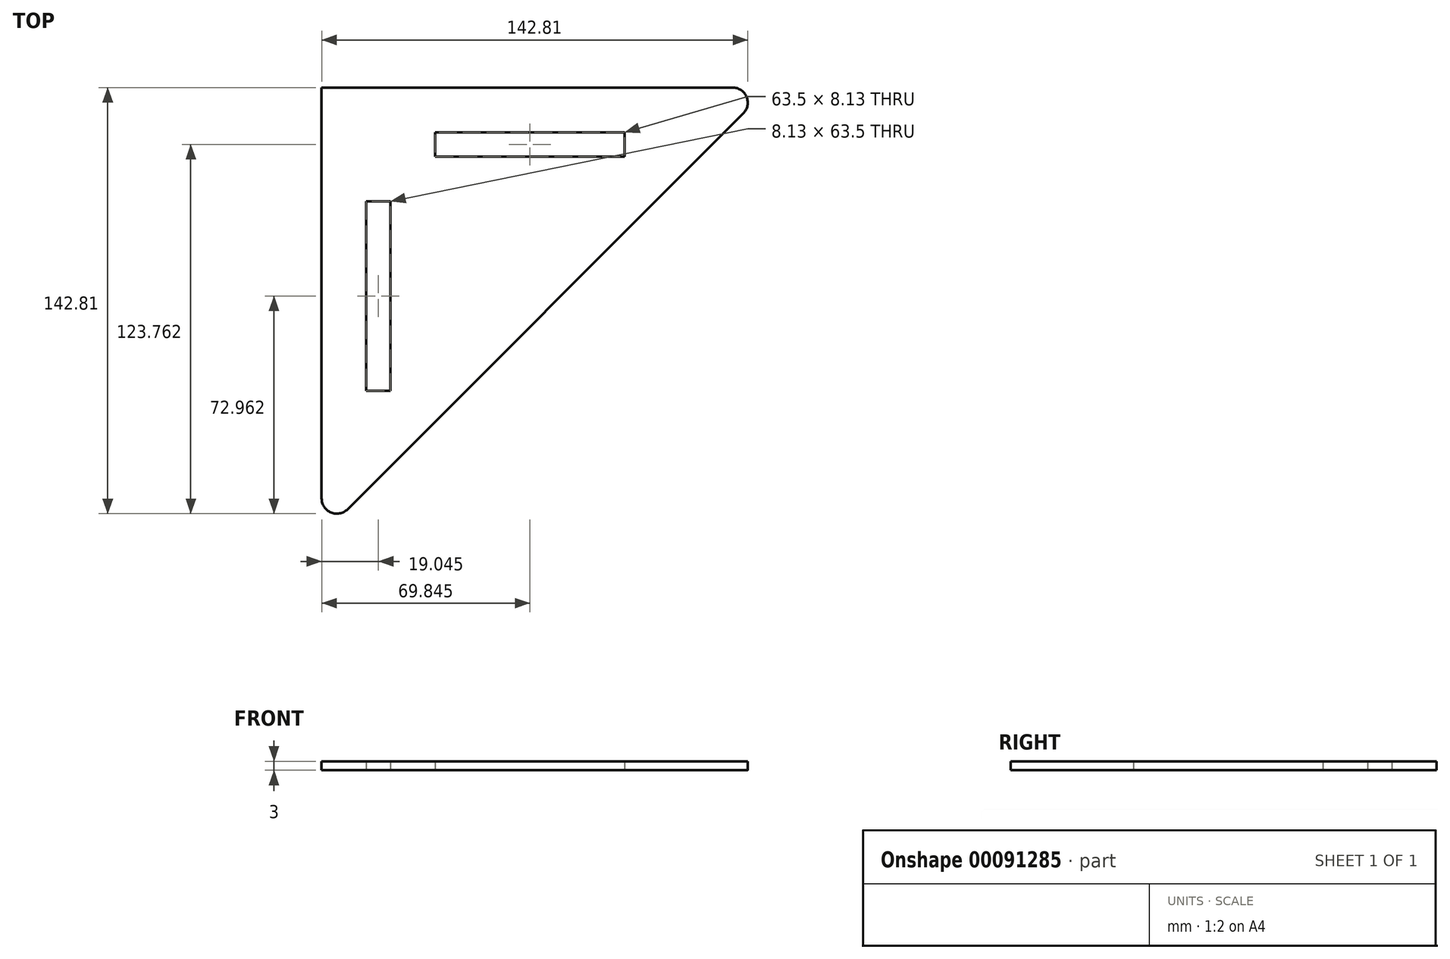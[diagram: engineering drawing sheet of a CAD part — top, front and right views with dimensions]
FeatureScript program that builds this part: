
annotation { "Feature Type Name" : "Feature", "Feature Type Description" : "" }
export const myFeature = defineFeature(function(context is Context, id is Id, definition is map)
    precondition{}
    {
        {
            var Q0;
            Q0=qCreatedBy(makeId("Top.planeOp"),FACE);
            var sketch = newSketch(context, id + "F0", { "sketchPlane" : qUnion([Q0])});
            skLineSegment(sketch, "E0", {"start": v(-72.91, 76.75) * mm, "end": v(-72.91, -73.25) * mm});
            skLineSegment(sketch, "E1", {"start": v(-72.91, -73.25) * mm, "end": v(77.09, 76.75) * mm});
            skLineSegment(sketch, "E2", {"start": v(77.09, 76.75) * mm, "end": v(-72.91, 76.75) * mm});
            skLineSegment(sketch, "E3.bottom", {"start": v(-57.93, 38.65) * mm, "end": v(-49.8, 38.65) * mm});
            skLineSegment(sketch, "E3.top", {"start": v(-57.93, -24.85) * mm, "end": v(-49.8, -24.85) * mm});
            skLineSegment(sketch, "E3.left", {"start": v(-57.93, 38.65) * mm, "end": v(-57.93, -24.85) * mm});
            skLineSegment(sketch, "E3.right", {"start": v(-49.8, 38.65) * mm, "end": v(-49.8, -24.85) * mm});
            skLineSegment(sketch, "E4.bottom", {"start": v(-34.81, 61.77) * mm, "end": v(28.69, 61.77) * mm});
            skLineSegment(sketch, "E4.top", {"start": v(-34.81, 53.64) * mm, "end": v(28.69, 53.64) * mm});
            skLineSegment(sketch, "E4.left", {"start": v(-34.81, 61.77) * mm, "end": v(-34.81, 53.64) * mm});
            skLineSegment(sketch, "E4.right", {"start": v(28.69, 61.77) * mm, "end": v(28.69, 53.64) * mm});
            skSolve(sketch);
        }
        {
            var Q0;
            Q0=makeQuery(id+"F0.imprint","IMPRINT",FACE,{"disambiguationData":[TD([[makeQuery(id+"F0.imprint","IMPRINT",EDGE,{"derivedFrom":sQuery(id+"F0.wireOp",EDGE,"E0")}),1.0]])]});
            extrude(context, id + "F1", {"entities" : qUnion([Q0]), "depth" : 3 * mm});
        }
        {
            var Q0;
            Q0=makeQuery(id+"F1.opExtrude","SWEPT_EDGE",EDGE,{"disambiguationData":[OSD([sQuery(id+"F0.wireOp",EDGE,"E0"),sQuery(id+"F0.wireOp",EDGE,"E1")])]});
            var Q1;
            Q1=makeQuery(id+"F1.opExtrude","SWEPT_EDGE",EDGE,{"disambiguationData":[OSD([sQuery(id+"F0.wireOp",EDGE,"E1"),sQuery(id+"F0.wireOp",EDGE,"E2")])]});
            fillet(context, id + "F2", {"entities" : qUnion([Q0, Q1]), "radius" : 5.08 * mm, "tangentPropagation" : true, "allowEdgeOverflow" : false});
        }
    });
